# Revit family: D20095001
name_source: partatom
category: Plumbing Fixtures
revit_build: Autodesk Revit 2014 (Build: 20130308_1515(x64)
units: mm (PartAtom-declared; Revit-internal decimal feet)

## types (2) — shared parameters
Assembly Code = D2010310
Basin Shape = Rectangle
CW Connection = Yes
CWFU = 1.5
Cold Water Connection Diameter = 1/2"
Cold Water Connection Height = 24 3/4"
Cold Water Connection Radius = 1/4"
Cold Water Connection Width = 4"
Default Elevation = 34"
HW Connection = Yes
HWFU = 1.5
Height = 4 3/4"
Hot Water Connection Diameter = 1/2"
Hot Water Connection Height = 24 3/4"
Hot Water Connection Radius = 1/4"
Hot Water Connection Width = 4"
Installation Type = Wall-Mounted
Length = 22"
Manufacturer = DXV
Material = Fine Fire Clay-DXV-415-Canvas White
Price = Prices may vary. Please consult Manufacturer Representative for most up-to-date price list.
Product Documentation Link = https://dxv01.blob.core.windows.net
Product Page URL = https://www.dxv.com
URL = https://www.dxv.com
Vent Connection = No
WFU = 2
Warranty Documentation Link = https://www.dxv.com
Waste Connection = Yes
Waste Connection Diameter = 1 1/4"
Waste Connection Height = 23"
Waste Connection Radius = 5/8"
Width = 24"

## per-type parameters (varying)
| type | 3 Hole Faucet | Description | Model | Single/Three Faucet Hole |
| D20095001.415 | No | Cossu 24 Inch Pedestal Bathroom Sink- Single Faucet Hole | D20095001.415 | -1 1/4" |
| D20095008.415 | Yes | Cossu 24 Inch Pedestal Bathroom Sink- 3 Faucet Hole | D20095008.416 | 2 1/4" |

## geometry (parser evidence)
native form markers: Sweep x2
no freeform markers — native parametric forms only
